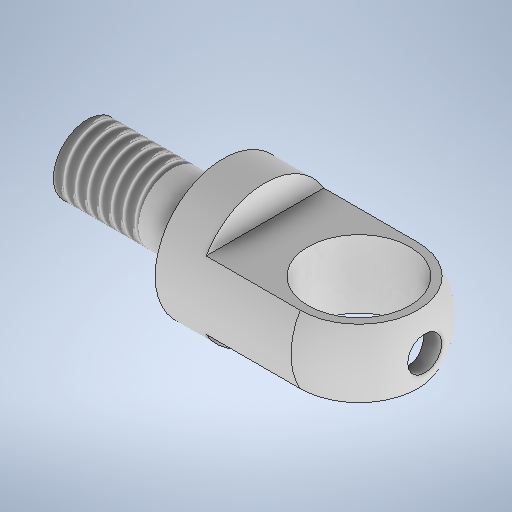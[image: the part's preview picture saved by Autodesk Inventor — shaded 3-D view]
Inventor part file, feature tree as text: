
AUTODESK INVENTOR PART (.ipt)
format: ipt  version: 2025.1 (Build 291241000, 241)  size: 314,880 bytes
history: native  units: mm
features: sketch x4, plane x2, hole x2, revolve x1, thread x1, extrude x1
ambient origin geometry x8: Origin, YZ Plane, XZ Plane, XY Plane, X Axis, Y Axis, Z Axis, Center Point
bodies: Solid1 (feature_tree)
feature tree (11):
  revolve  "Revolution1"  [1 undecoded]
  thread  "Thread1"  [1 undecoded]
  plane  "Work Plane2"
  extrude  "Extrusion1"  Depth=8.0mm
  hole  "Hole1"  [1 undecoded]
  plane  "Work Plane3"
  hole  "Hole2"  [1 undecoded]
  sketch  "Sketch1"  dims[d0=4.0mm d1=8.0mm d2=8.0mm]
  sketch  "Sketch3"  dims[d3=4.0mm d4=8.0mm]
  sketch  "Sketch4"  dims[d5=90.0deg d6=11.0mm d7=3.0mm]
  sketch  "Sketch5"  dims[d9=4.0mm d10=9.0mm d11=4.0mm d12=2.0mm d13=8.0mm d14=0.0mm d15=6.0mm d16=14.0mm d17=4.0mm d18=2.0mm d19=90.0deg d20=8.0mm d21=0.0mm d22=20.0mm d23=2.0mm d24=6.0mm d25=4.0mm d26=2.0mm d27=90.0deg d28=2.5mm d29=0.0mm]
note: 4 required parameter values undecoded (feature->parameter linkage not recoverable at this tier; creation-order binding heuristic only, values carry confidence <= 0.55)